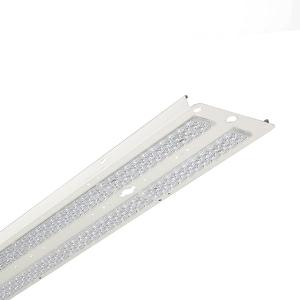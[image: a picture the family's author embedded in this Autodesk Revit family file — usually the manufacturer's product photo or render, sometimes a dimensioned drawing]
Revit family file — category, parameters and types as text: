
# Revit family: 3f_filippi_-_kit_led_retrofit_per_schermo_in_vetro_3f_filippi_-_a5210_a5184_-_kit_led_i3f_76_a3f_91_-_l1_1f837a277b034cc8
name_source: partatom
category: Lighting Fixtures
units: mm (PartAtom-declared; Revit-internal decimal feet)

## family parameters
Cut with Voids When Loaded = No
Host = Face
Light Source = No
Part Type = Normal
Room Calculation Point = No
Round Connector Dimension = Use Diameter
Shared = No

## types (1)
- 3F Filippi - Kit LED Retrofit per schermo in vetro (1 x LED, 10035 lm, 74 W, 4000 K)
    Apparent Load = 74 VA
    Approval mark = ENEC
    CIE Flux Codes = 68 92 98 100 100
    Color Rendering = 80
    Color Temperature = 4000 K
    Control Gear = Electronic ballast
    Default Elevation = 1800 mm
    Description = Led retrofit kit suitable for Fluorescent Beta 2x i3F 75 and A3F 90 luminaires.

ILLUMINOTECHNICAL
Luminous efficiency 100% (DLOR 100%, ULOR 0%).
Initial luminous flux of the luminaire 10035 lm.
Wide symmetric distribution.
Installation Interdistance Transv.D = 1.31 x hu - Long.D = 1.36 x hu.
Tabular UGR (CIE 117 - 4H-8H; S=0.25H; 70/50/20): RUG 19.4 - 20.6.
Beam angle: 85° - 89°.
Luminous efficacy 136 lm/W.
Lifetime (L93/B10): 30000 h. (tq+25°C)
Lifetime (L90/B10): 50000 h. (tq+25°C)
Lifetime (L85/B10): 80000 h. (tq+25°C)
Lifetime (L80/B10): 100000 h. (tq+25°C)
Lifetime (L85/B10): 50000 h. (tq+40°C)
Sudden decreased luminous flux after 50000 hours: 0% (C0).
Photobiological safety in compliance with IEC/TR 62778: RG0 risk exempt, (IEC 62471).
In compliance with IEC/EN 62722-2-1 - IEC/EN 62717 standards.

SOURCE
2 linear LED modules 40W/840.
Energy efficiency class (UE 2019/2020 - UE 2019/2015): C.
CIE 13.3 Colour rendering index: CRI >80 (R9 <50%).
IES TM-30 Fidelity Index: Rf = 84 Rg = 95.
CCT nominal colour temperature 4000 K.
Colour initial tolerance (MacAdam): SDCM 3.

MECHANICAL
Gear-tray unit in hot-galvanised steel, painted in white polyester, fixed to the housing by means of "Ribloc" rapid devices in galvanised steel, hinged opening.
Lenses for wide distribution, in transparent methacrylate (PMMA) with external flat surface.
Luminaire with limited surface temperature. - D - (EN 60598-2-24)
Dimensions: 1565x235 mm, height 105 mm. Weight 8.117 kg.
Glow-wire test resistance 850°C.

ELECTRICAL
Halogen Free electronic wiring 230V-50/60Hz, power factor 0.95, THD <25%, constant output current, class I, 1 driver.
Power of the luminaire 74 W.
CE - IEC 60598-1 - EN 60598-1.
SAFE FLICKER: PstLM=<1 and SVM=<0.4 (IEC TR 61547-1 and IEC TR 63158), to ensure a more comfortable and safe light.
Luminaire compliant with EN 60598-2-22 for power supply from a centralised emergency system CPSS (Central Power Supply System), not incorporated in the luminaire - high risk areas excluded. The default power and flux are 100% in AC and 100% in DC.
Ambient temperature from -20°C to +40°C.
Temperature class T6 max 85°C.
Relative humidity UR: <85%.

INSTALLATION
Retrofit.
Correct installation of the retrofit LED kit, compliant with EN 60598-1 and CE marked, inside the 3F Filippi - Beta 2x i3F 76 and A3F 91 Fluorescent luminaires must be only carried out by qualified personnel to ensure compliance with the national installation standards.
Attention: to maintain the degree of protection of the device and for the purposes of validity of the guarantee of the new retrofit kits, it is imperative to replace the old cable guides (on the body of the device) with the new ones supplied.
All accessories dedicated to this product are available on the Catalog and on our website www.3F-Filippi.com.

ACCESSORIES
A5184 - Printed glass Beta 2x i3F 76 - L1565.

WARNING
Fixture not suitable for cold stores with an ambient temperature <0°C and/or relative humidity >85%.
Luminaire designed for disposal/recycling at end-of-life.
Replaceable (LED only) light source by a professional. Replaceable control gear by a professional.
    Height = 105 mm
    Lamp = 1 x LED
    Lamp Light Flux = 10035 lm
    Lamp Power = 74 W
    Lamp count = 1
    Length = 1565 mm
    Lifetime = 50000 h
    Luminous efficacy = 136 lm/W
    Manufacturer = 3F Filippi
    ModVariant = No
    Model = 3F Filippi - A5210+A5184 - Kit LED i3F 76,A3F 91 - L1565 - L 2x40W AMPIO + VS
    Mounting Place = Ceiling
    Mounting Type = Surface mounted
    Number of Poles = 1
    OnlyDefault = Yes
    Power Factor = 1
    Product Name = 3F Filippi - Kit LED Retrofit per schermo in vetro
    Product group = ceiling mounted luminaire
    ProductGroupID = 3
    Protection Class = Protection class I
    Protection Degree = Degree of protection
    RLX_Detail_Level = 1
    RLX_Emergency_Light_Flux = 0 lm
    RLX_Emergency_Type = 0
    RLX_Emergency_Type_DB = No
    RlxData = <blob elided: 69889 chars, md5=c15cdc4b>
    Socket = socket
    Standby Power = 0 W
    System Light Flux = 10035 lm
    System Power = 74 W
    Type Comments = Product without accessories
    Type Image = 3ffilippi_a5210_a5184.jpg
    URL = http://relux.com
    VarID = ---
    Voltage = 0 V
    Weight = 0.00 kg
    Width = 235 mm

## geometry (parser evidence)
native form markers: Blend x4, Sweep x10
no freeform markers — native parametric forms only
